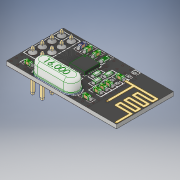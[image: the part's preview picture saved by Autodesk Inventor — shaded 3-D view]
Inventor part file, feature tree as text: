
AUTODESK INVENTOR PART (.ipt)
format: ipt  version: 2019.4 (Build 234330000, 330)  size: 6,975,488 bytes
history: mixed  units: mm
features: other x99, loft x29, boolean_combine x2, imported_body x1
ambient origin geometry x8: Origin, YZ Plane, XZ Plane, XY Plane, X Axis, Y Axis, Z Axis, Center Point
bodies: Solid1 (imported_parasolid), Solid2 (imported_parasolid), Solid3 (imported_parasolid), Solid4 (imported_parasolid), Solid5 (imported_parasolid), Solid6 (imported_parasolid), Solid7 (imported_parasolid), Solid8 (imported_parasolid), Solid9 (imported_parasolid), Solid10 (imported_parasolid), Solid11 (imported_parasolid), Solid12 (imported_parasolid), Solid13 (imported_parasolid), Solid14 (imported_parasolid), Solid15 (imported_parasolid), Solid16 (imported_parasolid), Solid17 (imported_parasolid), Solid18 (imported_parasolid), Solid19 (imported_parasolid), Solid20 (imported_parasolid), Solid21 (imported_parasolid), Solid22 (imported_parasolid), Solid23 (imported_parasolid), Solid24 (imported_parasolid), Solid25 (imported_parasolid), Solid26 (imported_parasolid), Solid27 (imported_parasolid), Solid28 (imported_parasolid), Solid29 (imported_parasolid), Solid30 (imported_parasolid), Solid31 (imported_parasolid), Solid32 (imported_parasolid), Solid33 (imported_parasolid), Solid34 (imported_parasolid), Solid35 (imported_parasolid), Solid36 (imported_parasolid), Solid37 (imported_parasolid), Solid38 (imported_parasolid), Solid39 (imported_parasolid), Solid40 (imported_parasolid), Solid41 (imported_parasolid), Solid42 (imported_parasolid), Solid43 (imported_parasolid), Solid44 (imported_parasolid), Solid45 (imported_parasolid), Solid46 (imported_parasolid), Solid47 (imported_parasolid), Solid48 (imported_parasolid), Solid49 (imported_parasolid), Solid50 (imported_parasolid), Solid51 (imported_parasolid), Solid52 (imported_parasolid), Solid53 (imported_parasolid), Solid54 (imported_parasolid), Solid55 (imported_parasolid), Solid56 (imported_parasolid), Solid57 (imported_parasolid), Solid58 (imported_parasolid), Solid59 (imported_parasolid), Solid60 (imported_parasolid), Solid61 (imported_parasolid), Solid62 (imported_parasolid), Solid63 (imported_parasolid), Solid64 (imported_parasolid), Solid65 (imported_parasolid), Solid66 (imported_parasolid), Solid67 (imported_parasolid), Solid68 (imported_parasolid), Solid69 (imported_parasolid), Solid70 (imported_parasolid), Solid71 (imported_parasolid), Solid72 (imported_parasolid), Solid73 (imported_parasolid), Solid74 (imported_parasolid), Solid75 (imported_parasolid), Solid76 (imported_parasolid), Solid77 (imported_parasolid), Solid78 (imported_parasolid), Solid79 (imported_parasolid), Solid80 (imported_parasolid), Solid81 (imported_parasolid), Solid82 (imported_parasolid), Solid83 (imported_parasolid), Solid84 (imported_parasolid), Solid85 (imported_parasolid), Solid86 (imported_parasolid), Solid87 (imported_parasolid), Solid88 (imported_parasolid), Solid89 (imported_parasolid), Solid90 (imported_parasolid), Solid91 (imported_parasolid), Solid92 (imported_parasolid), Solid93 (imported_parasolid), Solid94 (imported_parasolid), Solid95 (imported_parasolid), Solid96 (imported_parasolid), Solid97 (imported_parasolid), Solid98 (imported_parasolid), Solid99 (imported_parasolid), Solid100 (imported_parasolid), Solid101 (imported_parasolid), Solid102 (imported_parasolid), Solid103 (imported_parasolid), Solid104 (imported_parasolid), Solid105 (imported_parasolid), Solid106 (imported_parasolid), Solid107 (imported_parasolid), Solid108 (imported_parasolid), Solid109 (imported_parasolid), Solid110 (imported_parasolid), Solid111 (imported_parasolid), Solid112 (imported_parasolid), Solid113 (imported_parasolid), Solid114 (imported_parasolid), Solid115 (imported_parasolid), Solid116 (imported_parasolid), Solid117 (imported_parasolid), Solid118 (imported_parasolid), Solid119 (imported_parasolid), Solid120 (imported_parasolid), Solid121 (imported_parasolid), Solid122 (imported_parasolid), Solid123 (imported_parasolid), Solid124 (imported_parasolid), Solid125 (imported_parasolid), Solid126 (imported_parasolid), Solid127 (imported_parasolid), Solid128 (imported_parasolid), Solid129 (imported_parasolid), Solid130 (imported_parasolid)
feature tree (131):
  other  "PCB Body"
  other  "Cut-Extrude1[2]"
  other  "Cut-Extrude1[3]"
  other  "Cut-Extrude1[4]"
  other  "Cut-Extrude1[5]"
  other  "Cut-Extrude1[6]"
  other  "Cut-Extrude1[7]"
  other  "Cut-Extrude1[8]"
  other  "Cut-Extrude1[9]"
  other  "Cut-Extrude1[10]"
  other  "Cut-Extrude1[11]"
  other  "Cut-Extrude1[12]"
  other  "Cut-Extrude1[13]"
  other  "Cut-Extrude2[1]"
  other  "Cut-Extrude2[2]"
  other  "Cut-Extrude2[3]"
  other  "Cut-Extrude2[4]"
  other  "_Capacitor 1608_-_Solid7_"
  other  "Body-Move_Copy21"
  other  "Body-Move_Copy22"
  other  "_Resistor 1608_-_Imported1_"
  other  "Body-Move_Copy26"
  other  "Body-Move_Copy28"
  other  "Body-Move_Copy29[1]"
  other  "Body-Move_Copy29[2]"
  other  "Body-Move_Copy30"
  other  "Body-Move_Copy31"
  other  "Body-Move_Copy34"
  other  "_rg1608p-103-b_-_rg1608p-103-b_"
  other  "Body-Move_Copy38"
  other  "Body-Move_Copy39"
  other  "_QFN-20 with Pad_-_Вытянуть4_"
  other  "Boss-Extrude22"
  other  "Boss-Extrude28"
  other  "Body-Move_Copy50"
  other  "Boss-Extrude31"
  other  "Cut-Extrude3"
  loft  "Loft2"
  loft  "Loft4"
  loft  "Loft7"
  loft  "Loft9"
  loft  "Loft10"
  loft  "Loft12"
  loft  "Loft13"
  loft  "Loft14"
  loft  "Loft15"
  loft  "Loft16"
  loft  "Loft17"
  loft  "Loft18"
  loft  "Loft19"
  loft  "Loft20"
  loft  "Loft21"
  loft  "Loft22"
  loft  "Loft23"
  loft  "Loft24"
  loft  "Loft25"
  loft  "Loft26"
  loft  "Loft27"
  loft  "Loft28"
  loft  "Loft29"
  loft  "Loft30"
  loft  "Loft31"
  loft  "Loft32"
  loft  "Loft33"
  loft  "Loft34"
  loft  "Loft35"
  other  "Body-Move_Copy51[1]"
  other  "Body-Move_Copy51[2]"
  other  "Body-Move_Copy51[3]"
  other  "Body-Move_Copy51[4]"
  other  "Body-Move_Copy53[1]"
  other  "Body-Move_Copy53[2]"
  other  "Body-Move_Copy53[3]"
  other  "Body-Move_Copy53[4]"
  other  "Body-Move_Copy53[5]"
  other  "Body-Move_Copy57[1]"
  other  "Body-Move_Copy57[2]"
  other  "Body-Move_Copy57[3]"
  other  "Body-Move_Copy57[4]"
  other  "Body-Move_Copy57[5]"
  other  "Body-Move_Copy57[6]"
  other  "Body-Move_Copy57[7]"
  other  "Body-Move_Copy57[8]"
  other  "Body-Move_Copy57[9]"
  other  "Body-Move_Copy57[10]"
  other  "Boss-Extrude38[1]"
  other  "Boss-Extrude38[2]"
  other  "Boss-Extrude38[3]"
  other  "Boss-Extrude38[4]"
  other  "Cut-Extrude4[1]"
  other  "Cut-Extrude4[2]"
  other  "_Header 2_54 Vertical 1x2_-_Chamfer2_"
  other  "Cut-Extrude5[1]"
  other  "Cut-Extrude5[2]"
  other  "Cut-Extrude5[3]"
  other  "Cut-Extrude5[4]"
  other  "Cut-Extrude5[5]"
  other  "Cut-Extrude5[6]"
  other  "Cut-Extrude5[7]"
  other  "Cut-Extrude5[8]"
  other  "Boss-Extrude43"
  other  "Boss-Extrude45[1]"
  other  "Boss-Extrude45[2]"
  other  "Boss-Extrude45[3]"
  other  "Boss-Extrude45[4]"
  other  "Boss-Extrude45[5]"
  other  "Boss-Extrude45[6]"
  other  "Boss-Extrude45[7]"
  other  "Boss-Extrude45[8]"
  other  "Boss-Extrude45[9]"
  other  "Boss-Extrude45[10]"
  other  "Boss-Extrude45[11]"
  other  "Boss-Extrude45[12]"
  other  "Boss-Extrude45[13]"
  other  "Boss-Extrude45[14]"
  other  "Boss-Extrude45[15]"
  other  "Boss-Extrude45[16]"
  other  "Boss-Extrude45[17]"
  other  "Boss-Extrude45[18]"
  other  "Boss-Extrude45[19]"
  other  "Boss-Extrude45[20]"
  other  "Boss-Extrude45[21]"
  other  "Boss-Extrude45[22]"
  other  "Boss-Extrude45[23]"
  other  "Boss-Extrude45[24]"
  boolean_combine  "Combine15"
  boolean_combine  "Combine16"
  other  "LPattern2[1]"
  other  "LPattern2[2]"
  other  "LPattern2[3]"
  imported_body  NMx_Import_Brep_tag  [imported B-rep: ~538 faces, bbox_mm=None]
